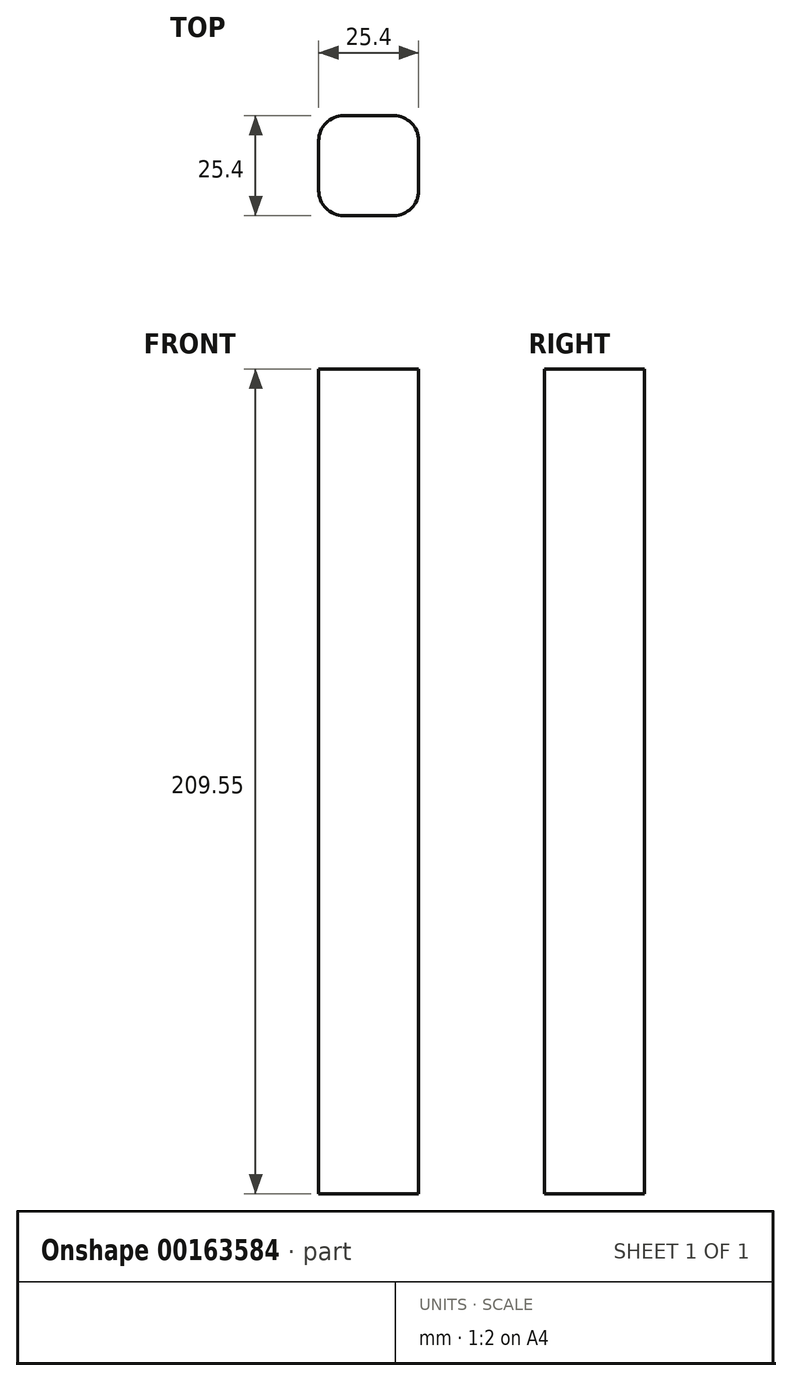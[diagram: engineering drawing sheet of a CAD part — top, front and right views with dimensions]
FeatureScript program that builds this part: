
annotation { "Feature Type Name" : "Feature", "Feature Type Description" : "" }
export const myFeature = defineFeature(function(context is Context, id is Id, definition is map)
    precondition{}
    {
        {
            var Q0;
            Q0=qCreatedBy(makeId("Top.planeOp"),FACE);
            var sketch = newSketch(context, id + "F0", { "sketchPlane" : qUnion([Q0])});
            skLineSegment(sketch, "E0.bottom", {"start": v(12.7, 12.7) * mm, "end": v(-12.7, 12.7) * mm});
            skLineSegment(sketch, "E0.top", {"start": v(12.7, -12.7) * mm, "end": v(-12.7, -12.7) * mm});
            skLineSegment(sketch, "E0.left", {"start": v(12.7, 12.7) * mm, "end": v(12.7, -12.7) * mm});
            skLineSegment(sketch, "E0.right", {"start": v(-12.7, 12.7) * mm, "end": v(-12.7, -12.7) * mm});
            skPoint(sketch, "E0.middle", {"position": v(0, 0) * mm});
            skSolve(sketch);
        }
        {
            var Q0;
            Q0=qSketchRegion(id+"F0",true);
            extrude(context, id + "F1", {"entities" : qUnion([Q0]), "depth" : 209.55 * mm});
        }
        {
            var Q0;
            Q0=makeQuery(id+"F1.opExtrude","SWEPT_EDGE",EDGE,{"disambiguationData":[OSD([sQuery(id+"F0.wireOp",EDGE,"E0.top"),sQuery(id+"F0.wireOp",EDGE,"E0.left")])]});
            var Q1;
            Q1=makeQuery(id+"F1.opExtrude","SWEPT_EDGE",EDGE,{"disambiguationData":[OSD([sQuery(id+"F0.wireOp",EDGE,"E0.top"),sQuery(id+"F0.wireOp",EDGE,"E0.right")])]});
            var Q2;
            Q2=makeQuery(id+"F1.opExtrude","SWEPT_EDGE",EDGE,{"disambiguationData":[OSD([sQuery(id+"F0.wireOp",EDGE,"E0.bottom"),sQuery(id+"F0.wireOp",EDGE,"E0.right")])]});
            var Q3;
            Q3=makeQuery(id+"F1.opExtrude","SWEPT_EDGE",EDGE,{"disambiguationData":[OSD([sQuery(id+"F0.wireOp",EDGE,"E0.bottom"),sQuery(id+"F0.wireOp",EDGE,"E0.left")])]});
            fillet(context, id + "F2", {"entities" : qUnion([Q0, Q1, Q2, Q3]), "radius" : 6.35 * mm, "tangentPropagation" : true, "allowEdgeOverflow" : false});
        }
    });
